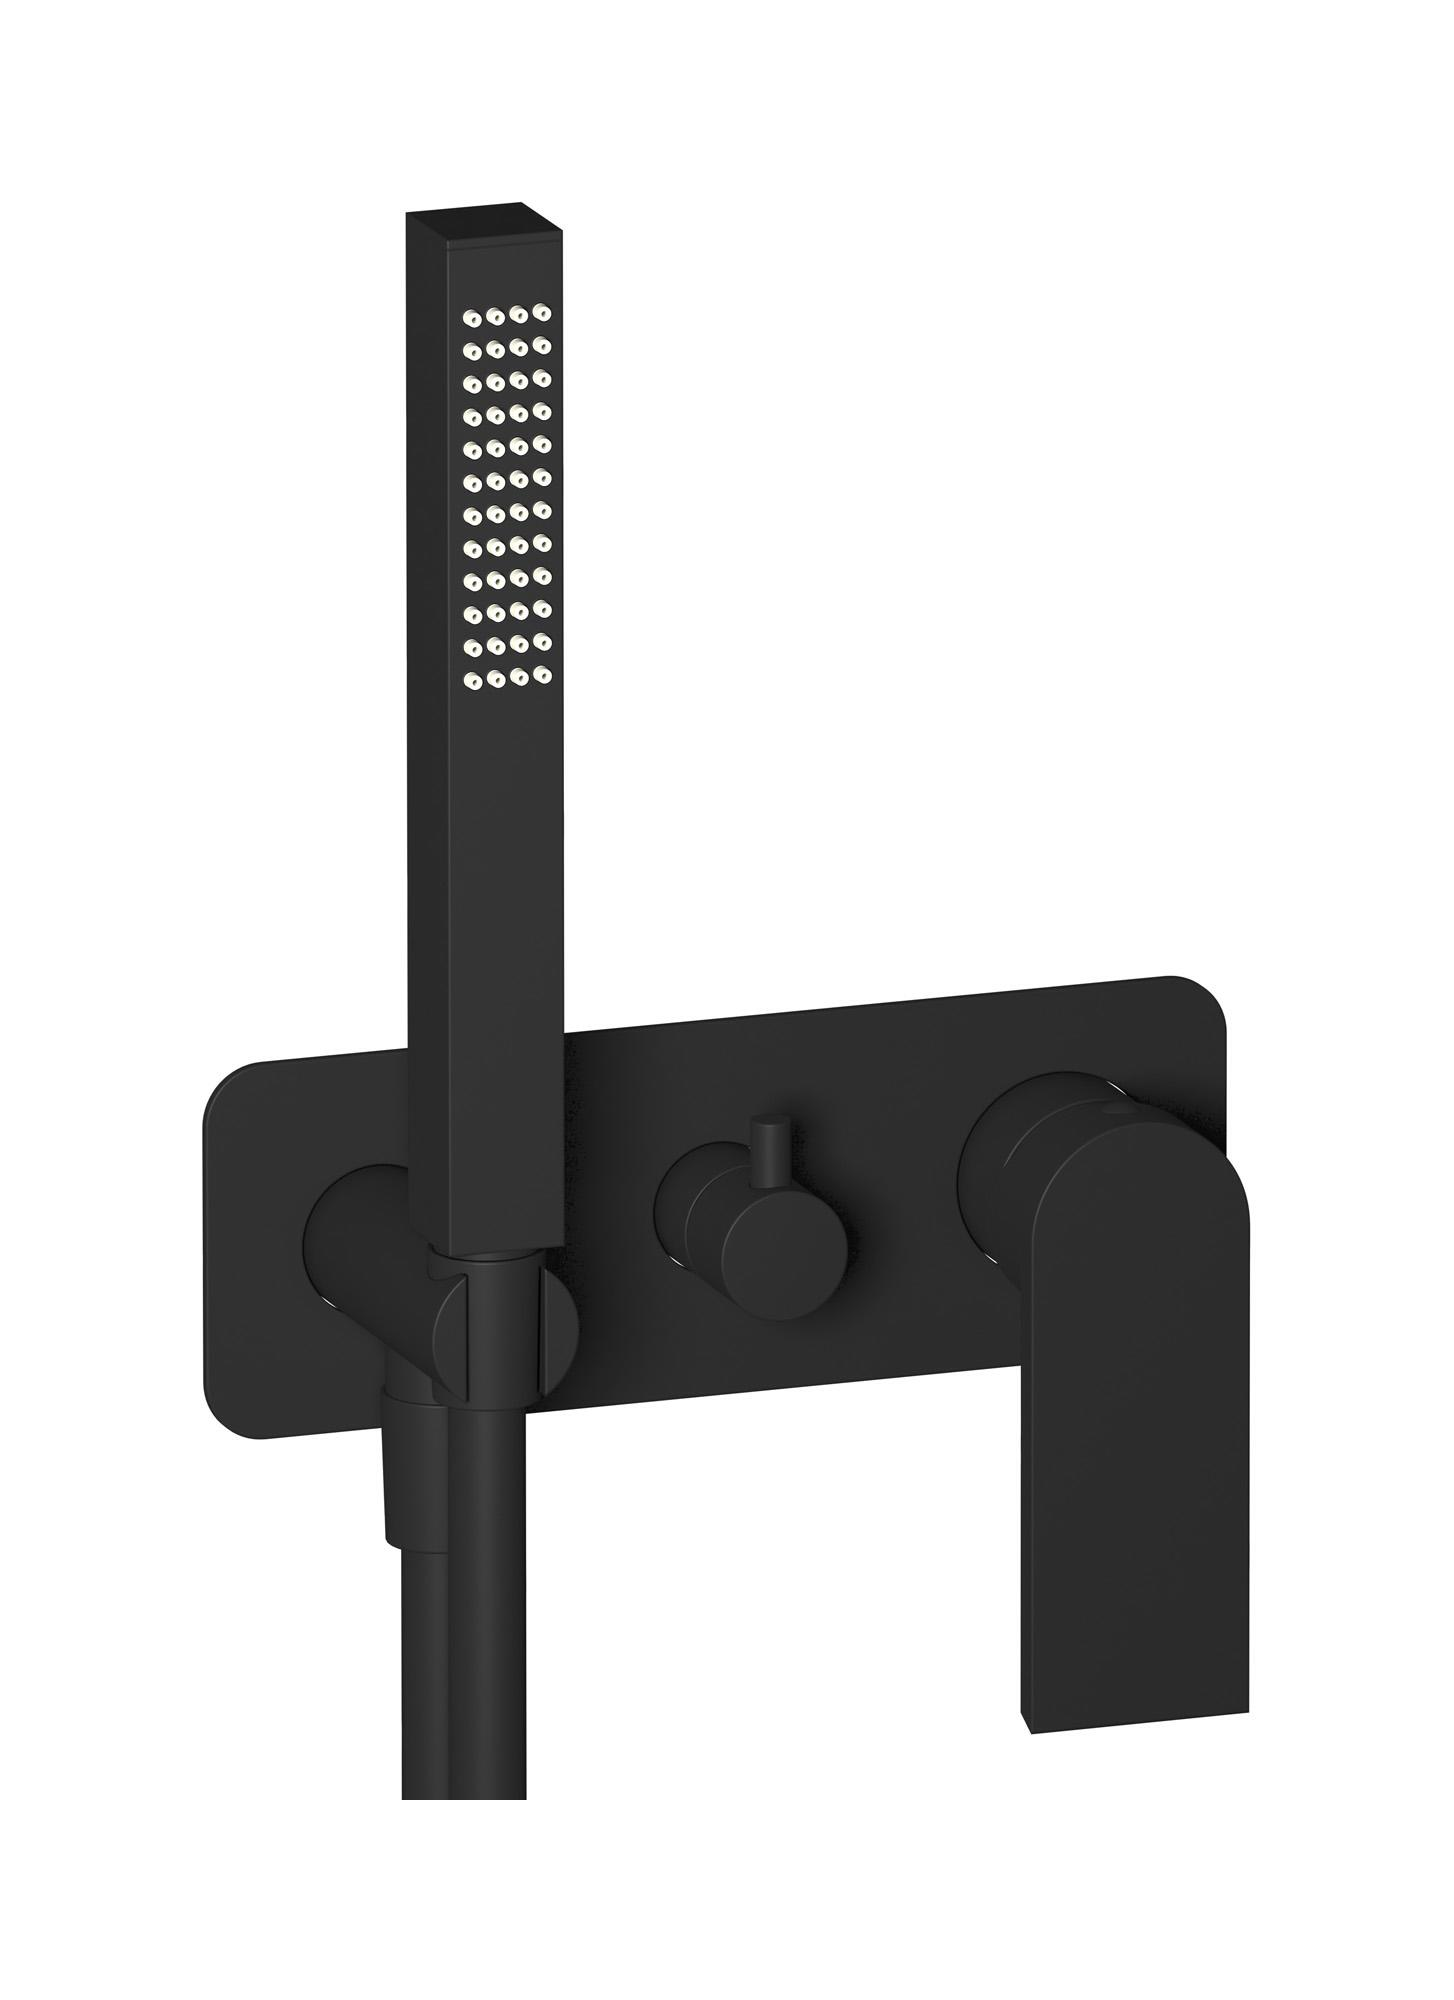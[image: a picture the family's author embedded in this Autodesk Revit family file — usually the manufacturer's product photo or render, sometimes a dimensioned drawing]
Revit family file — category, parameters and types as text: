
# Revit family: K3314
name_source: partatom
category: Apparecchi idraulici
units: mm (PartAtom-declared; Revit-internal decimal feet)

## family parameters
Basato su piano di lavoro = No
Condiviso = No
Mantieni orientamento annotazione = No
Numero OmniClass = 23.45.55.17
Punto di calcolo locali = No
Quota connettore circolare = Usa diametro
Sempre verticale = Sì
Taglio con vuoti quando caricato = No
Tipo di parte = Normale
Titolo OmniClass = Mixing Faucets

## types (8) — shared parameters
Cold water inlet = 10 mm  [stored 0.0328084 ft]
Commenti sul tipo = Wall mixer
Connessione CW = No
Connessione HW = No
Connessione di scarico = No
Connessione di ventilazione = No
Descrizione = Exposed parts for manual wall mixer with 3 ways diverter and shower kit
Hot water inlet = 10 mm  [stored 0.0328084 ft]
Produttore = IB Rubinetterie S.p.A.
URL = https://www.weareib.it
zero-valued in all types: Prospetto di default

## per-type parameters (varying)
| type | Finishes surface | Immagine tipo | Modello |
| Chrome | IB_Chrome | K3314CC.jpg | K3314CC |
| Brushed nickel | IB_Brushed nickel | K3314SS.jpg | K3314SS |
| Matt black | IB_matt black | K3314NP.jpg | K3314NP |
| Matt white | IB_matt white | K3314BO.jpg | K3314BO |
| Pale gold | IB_Pale gold | K3314II.jpg | K3314II |
| Brushed pale gold | IB_brushed pale gold | K3314IS.jpg | K3314IS |
| Rose gold | IB_Rose gold | K3314RS.jpg | K3314RS |
| Gold | IB_gold | K3314OO.jpg | K3314OO |

note: [stored X ft] marks values corroborated as IEEE doubles in the binary element streams (Revit-internal decimal feet)
